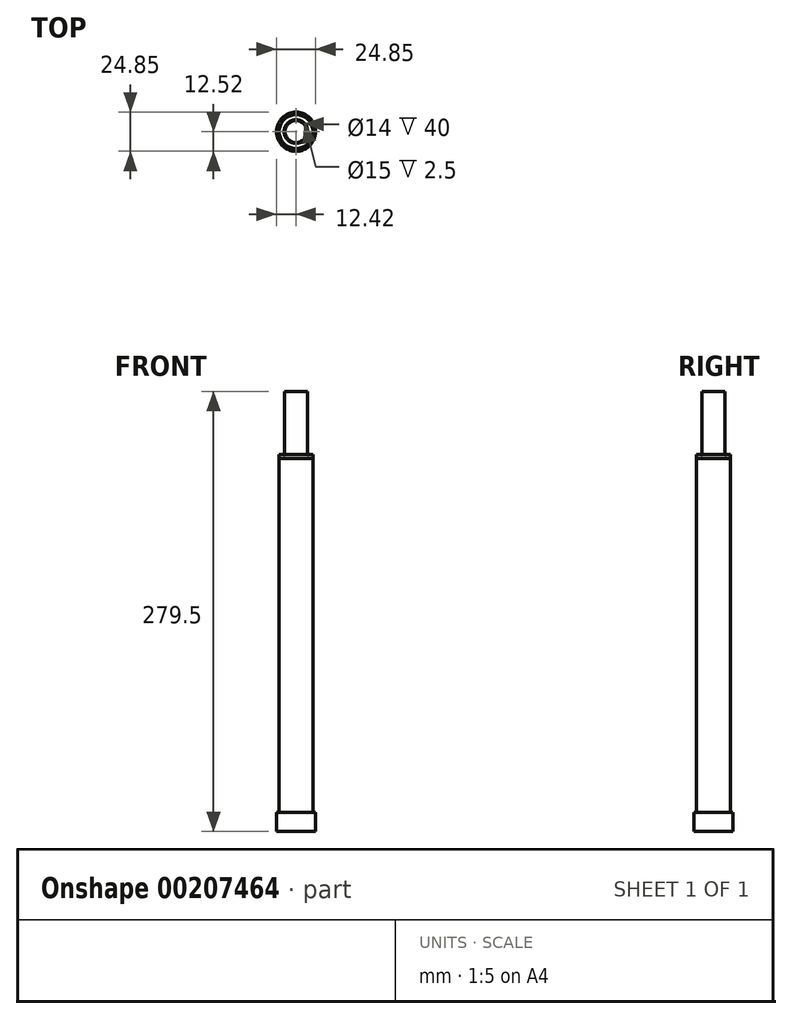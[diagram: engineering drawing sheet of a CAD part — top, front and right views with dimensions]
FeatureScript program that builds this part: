
annotation { "Feature Type Name" : "Feature", "Feature Type Description" : "" }
export const myFeature = defineFeature(function(context is Context, id is Id, definition is map)
    precondition{}
    {
        {
            var Q0;
            Q0=qCreatedBy(makeId("Top.planeOp"),FACE);
            var sketch = newSketch(context, id + "F0", { "sketchPlane" : qUnion([Q0])});
            skCircle(sketch, "E0", {"center": v(0, -0.1) * mm, "radius": 12.43 * mm});
            skSolve(sketch);
        }
        {
            var Q0;
            Q0 = qSketchRegion(id + "F0", true);
            extrude(context, id + "F1", {"entities" : qUnion([Q0]), "depth" : 12 * mm});
        }
        {
            var Q0;
            Q0=makeQuery(id+"F1.opExtrude","CAP_FACE",FACE,{"disambiguationData":[OSD([sQuery(id+"F0.wireOp",EDGE,"E0")])],"isStart":false});
            var sketch = newSketch(context, id + "F2", { "sketchPlane" : qUnion([Q0])});
            skCircle(sketch, "E1", {"center": v(0, 0) * mm, "radius": 10.78 * mm});
            skSolve(sketch);
        }
        {
            var Q0;
            Q0 = qSketchRegion(id + "F2", true);
            extrude(context, id + "F3", {"entities" : qUnion([Q0]), "operationType" : NewBodyOperationType.ADD, "depth" : 225 * mm});
        }
        {
            var Q0;
            Q0=makeQuery(id+"F3.opExtrude","CAP_FACE",FACE,{"disambiguationData":[OSD([sQuery(id+"F2.wireOp",EDGE,"E1")])],"isStart":false});
            var sketch = newSketch(context, id + "F4", { "sketchPlane" : qUnion([Q0])});
            skCircle(sketch, "E2", {"center": v(0, 0) * mm, "radius": 10.75 * mm});
            skCircle(sketch, "E3", {"center": v(0, 0) * mm, "radius": 7.5 * mm});
            skSolve(sketch);
        }
        {
            var Q0;
            Q0 = qSketchRegion(id + "F4", true);
            extrude(context, id + "F5", {"entities" : qUnion([Q0]), "operationType" : NewBodyOperationType.ADD, "depth" : 2.5 * mm});
        }
        {
            var Q0;
            Q0=makeQuery(id+"F5.opExtrude","CAP_FACE",FACE,{"disambiguationData":[OSD([sQuery(id+"F4.wireOp",EDGE,"E2"),sQuery(id+"F4.wireOp",EDGE,"E3")])],"isStart":false});
            var sketch = newSketch(context, id + "F6", { "sketchPlane" : qUnion([Q0])});
            skCircle(sketch, "E4", {"center": v(0, 0) * mm, "radius": 7.25 * mm});
            skCircle(sketch, "E5", {"center": v(0, 0) * mm, "radius": 7 * mm});
            skSolve(sketch);
        }
        {
            var Q0;
            Q0 = qSketchRegion(id + "F6", true);
            extrude(context, id + "F7", {"entities" : qUnion([Q0]), "operationType" : NewBodyOperationType.ADD, "depth" : 40 * mm});
        }
    });
